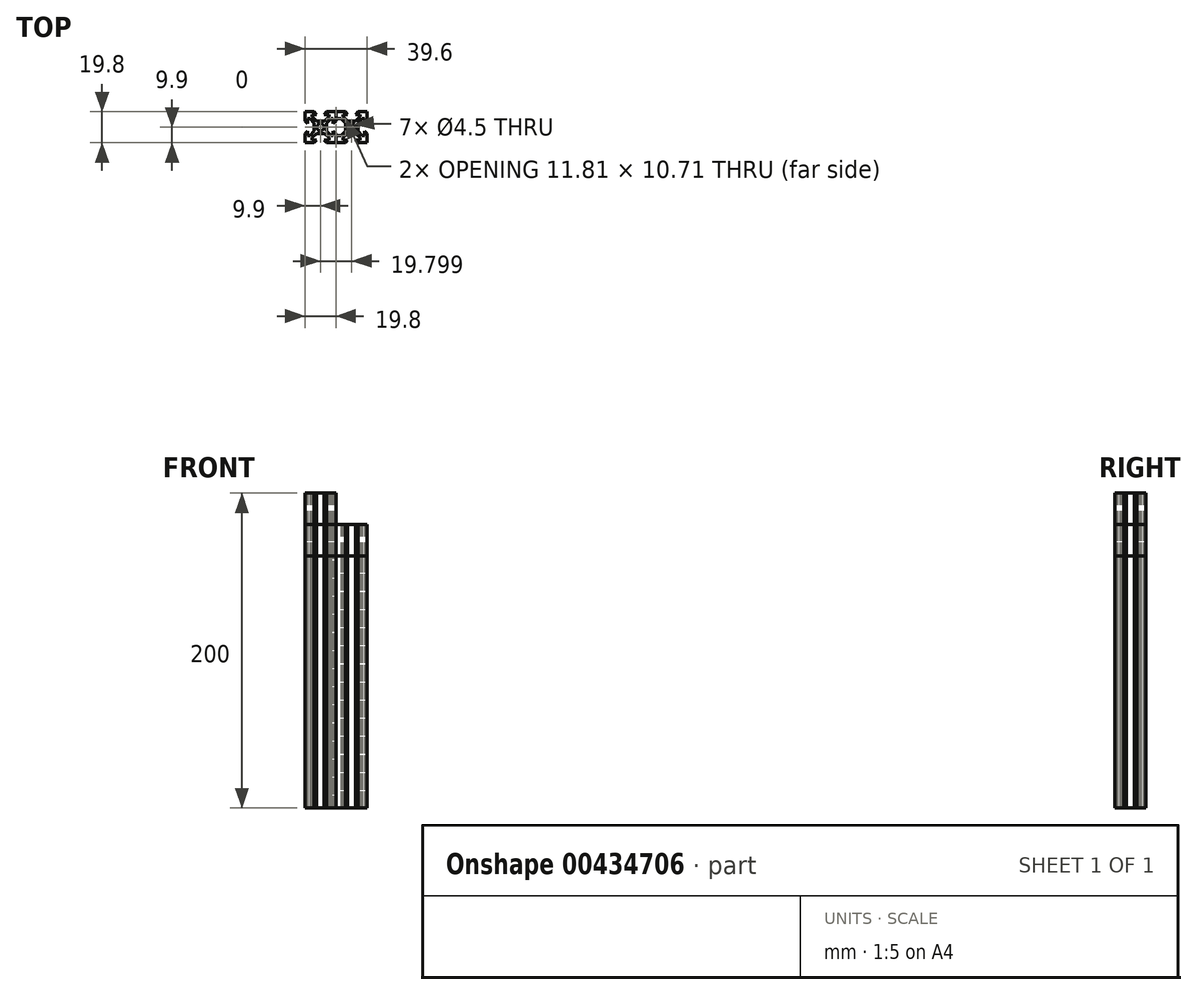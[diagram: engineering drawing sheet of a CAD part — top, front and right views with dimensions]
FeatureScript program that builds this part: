
annotation { "Feature Type Name" : "Feature", "Feature Type Description" : "" }
export const myFeature = defineFeature(function(context is Context, id is Id, definition is map)
    precondition{}
    {
        {
            assignVariable(context, id + "F0", {"name" : "Length", "anyValue" : 180});
        }
        {
            var Q0;
            Q0=qCreatedBy(makeId("Top.planeOp"),FACE);
            var sketch = newSketch(context, id + "F1", { "sketchPlane" : qUnion([Q0])});
            skCircle(sketch, "E0", {"center": v(0, 0) * mm, "radius": 2.25 * mm});
            skLineSegment(sketch, "E1", {"start": v(0, 82.59) * mm, "end": v(0, 0) * mm, "construction": true});
            skLineSegment(sketch, "E2", {"start": v(0, 0) * mm, "end": v(0, -82.59) * mm, "construction": true});
            skLineSegment(sketch, "E3", {"start": v(0, 0) * mm, "end": v(82.59, 0) * mm, "construction": true});
            skLineSegment(sketch, "E4", {"start": v(0, 0) * mm, "end": v(-82.59, 0) * mm, "construction": true});
            skLineSegment(sketch, "E5", {"start": v(0, 0) * mm, "end": v(-82.59, 82.59) * mm, "construction": true});
            skLineSegment(sketch, "E6", {"start": v(0, 0) * mm, "end": v(82.59, -82.59) * mm, "construction": true});
            skLineSegment(sketch, "E7", {"start": v(0, 0) * mm, "end": v(82.59, 82.59) * mm, "construction": true});
            skLineSegment(sketch, "E8", {"start": v(0, 0) * mm, "end": v(-82.59, -82.59) * mm, "construction": true});
            skLineSegment(sketch, "E9", {"start": v(-82.59, 82.59) * mm, "end": v(82.59, 82.59) * mm, "construction": true});
            skLineSegment(sketch, "E10", {"start": v(-82.59, -82.59) * mm, "end": v(82.59, -82.59) * mm, "construction": true});
            skLineSegment(sketch, "E11", {"start": v(-82.59, -82.59) * mm, "end": v(-82.59, 82.59) * mm, "construction": true});
            skLineSegment(sketch, "E12", {"start": v(82.59, -82.59) * mm, "end": v(82.59, 82.59) * mm, "construction": true});
            skPoint(sketch, "E13", {"position": v(-6.72, 6.72) * mm});
            skPoint(sketch, "E14", {"position": v(-4, 4) * mm});
            skPoint(sketch, "E15", {"position": v(-8.13, 8.13) * mm});
            skPoint(sketch, "E16", {"position": v(-47.98, 47.98) * mm});
            skPoint(sketch, "E17", {"position": v(-56.83, 56.83) * mm});
            skPoint(sketch, "E18", {"position": v(-9.9, 9.9) * mm});
            skLineSegment(sketch, "E19.bottom", {"start": v(-9.9, 9.9) * mm, "end": v(0, 9.9) * mm, "construction": true});
            skLineSegment(sketch, "E19.top", {"start": v(-9.9, 0) * mm, "end": v(0, 0) * mm, "construction": true});
            skLineSegment(sketch, "E19.left", {"start": v(-9.9, 9.9) * mm, "end": v(-9.9, 0) * mm, "construction": true});
            skLineSegment(sketch, "E19.right", {"start": v(0, 9.9) * mm, "end": v(0, 0) * mm, "construction": true});
            skLineSegment(sketch, "E20.MirrorCS", {"start": v(9.9, 9.9) * mm, "end": v(0, 9.9) * mm, "construction": true});
            skLineSegment(sketch, "E21.MirrorCS", {"start": v(9.9, 9.9) * mm, "end": v(9.9, 0) * mm, "construction": true});
            skLineSegment(sketch, "E22.MirrorCS", {"start": v(-9.9, -9.9) * mm, "end": v(-9.9, 0) * mm, "construction": true});
            skLineSegment(sketch, "E23.MirrorCS", {"start": v(-9.9, -9.9) * mm, "end": v(0, -9.9) * mm, "construction": true});
            skLineSegment(sketch, "E24.MirrorCS", {"start": v(9.9, -9.9) * mm, "end": v(0, -9.9) * mm, "construction": true});
            skLineSegment(sketch, "E25.MirrorCS", {"start": v(9.9, -9.9) * mm, "end": v(9.9, 0) * mm, "construction": true});
            skLineSegment(sketch, "E26.bottom", {"start": v(-4, 4) * mm, "end": v(0, 4) * mm, "construction": true});
            skLineSegment(sketch, "E26.top", {"start": v(-4, 0) * mm, "end": v(0, 0) * mm, "construction": true});
            skLineSegment(sketch, "E26.left", {"start": v(-4, 4) * mm, "end": v(-4, 0) * mm, "construction": true});
            skLineSegment(sketch, "E26.right", {"start": v(0, 4) * mm, "end": v(0, 0) * mm, "construction": true});
            skLineSegment(sketch, "E27.bottom", {"start": v(-6.72, 6.72) * mm, "end": v(0, 6.72) * mm, "construction": true});
            skLineSegment(sketch, "E27.top", {"start": v(-6.72, 0) * mm, "end": v(0, 0) * mm, "construction": true});
            skLineSegment(sketch, "E27.left", {"start": v(-6.72, 6.72) * mm, "end": v(-6.72, 0) * mm, "construction": true});
            skLineSegment(sketch, "E27.right", {"start": v(0, 6.72) * mm, "end": v(0, 0) * mm, "construction": true});
            skLineSegment(sketch, "E28.MirrorCS", {"start": v(4, 4) * mm, "end": v(0, 4) * mm, "construction": true});
            skLineSegment(sketch, "E29.MirrorCS", {"start": v(6.72, 6.72) * mm, "end": v(0, 6.72) * mm, "construction": true});
            skLineSegment(sketch, "E30.MirrorCS", {"start": v(6.72, 6.72) * mm, "end": v(6.72, 0) * mm, "construction": true});
            skLineSegment(sketch, "E31.MirrorCS", {"start": v(4, 4) * mm, "end": v(4, 0) * mm, "construction": true});
            skLineSegment(sketch, "E32.MirrorCS", {"start": v(-6.72, -6.72) * mm, "end": v(-6.72, 0) * mm, "construction": true});
            skLineSegment(sketch, "E33.MirrorCS", {"start": v(-4, -4) * mm, "end": v(-4, 0) * mm, "construction": true});
            skLineSegment(sketch, "E34.MirrorCS", {"start": v(-6.72, -6.72) * mm, "end": v(0, -6.72) * mm, "construction": true});
            skLineSegment(sketch, "E35.MirrorCS", {"start": v(-4, -4) * mm, "end": v(0, -4) * mm, "construction": true});
            skLineSegment(sketch, "E36.MirrorCS", {"start": v(4, -4) * mm, "end": v(0, -4) * mm, "construction": true});
            skLineSegment(sketch, "E37.MirrorCS", {"start": v(6.72, -6.72) * mm, "end": v(0, -6.72) * mm, "construction": true});
            skLineSegment(sketch, "E38.MirrorCS", {"start": v(6.72, -6.72) * mm, "end": v(6.72, 0) * mm, "construction": true});
            skLineSegment(sketch, "E39.MirrorCS", {"start": v(4, -4) * mm, "end": v(4, 0) * mm, "construction": true});
            skLineSegment(sketch, "E40.bottom", {"start": v(-6.72, 6.72) * mm, "end": v(-4, 6.72) * mm, "construction": true});
            skLineSegment(sketch, "E40.top", {"start": v(-6.72, 4) * mm, "end": v(-4, 4) * mm, "construction": true});
            skLineSegment(sketch, "E40.left", {"start": v(-6.72, 6.72) * mm, "end": v(-6.72, 4) * mm, "construction": true});
            skLineSegment(sketch, "E40.right", {"start": v(-4, 6.72) * mm, "end": v(-4, 4) * mm, "construction": true});
            skLineSegment(sketch, "E41.bottom", {"start": v(-9.9, 9.9) * mm, "end": v(-6.72, 9.9) * mm, "construction": true});
            skLineSegment(sketch, "E41.top", {"start": v(-9.9, 6.72) * mm, "end": v(-6.72, 6.72) * mm, "construction": true});
            skLineSegment(sketch, "E41.left", {"start": v(-9.9, 9.9) * mm, "end": v(-9.9, 6.72) * mm, "construction": true});
            skLineSegment(sketch, "E41.right", {"start": v(-6.72, 9.9) * mm, "end": v(-6.72, 6.72) * mm, "construction": true});
            skPoint(sketch, "E42.oppositeSnap0", {"position": v(-6.72, 5.36) * mm});
            skLineSegment(sketch, "E42.bottom", {"start": v(-9.9, 9.9) * mm, "end": v(-5.36, 9.9) * mm, "construction": true});
            skLineSegment(sketch, "E42.top", {"start": v(-9.9, 5.36) * mm, "end": v(-5.36, 5.36) * mm, "construction": true});
            skLineSegment(sketch, "E42.left", {"start": v(-9.9, 9.9) * mm, "end": v(-9.9, 5.36) * mm, "construction": true});
            skLineSegment(sketch, "E42.right", {"start": v(-5.36, 9.9) * mm, "end": v(-5.36, 5.36) * mm, "construction": true});
            skLineSegment(sketch, "E43.bottom", {"start": v(-5.36, 5.36) * mm, "end": v(-2.5, 5.36) * mm, "construction": true});
            skLineSegment(sketch, "E43.top", {"start": v(-5.36, 2.5) * mm, "end": v(-2.5, 2.5) * mm, "construction": true});
            skLineSegment(sketch, "E43.left", {"start": v(-5.36, 5.36) * mm, "end": v(-5.36, 2.5) * mm, "construction": true});
            skLineSegment(sketch, "E43.right", {"start": v(-2.5, 5.36) * mm, "end": v(-2.5, 2.5) * mm, "construction": true});
            skPoint(sketch, "E44", {"position": v(-5.36, 6.72) * mm});
            skPoint(sketch, "E45", {"position": v(-2.5, 4) * mm});
            skPoint(sketch, "E46", {"position": v(-4, 2.5) * mm});
            skPoint(sketch, "E47.MirrorP", {"position": v(5.36, 6.72) * mm});
            skPoint(sketch, "E48.MirrorP", {"position": v(2.5, 4) * mm});
            skPoint(sketch, "E49.MirrorP", {"position": v(4, 2.5) * mm});
            skPoint(sketch, "E50.MirrorP", {"position": v(6.72, 5.36) * mm});
            skPoint(sketch, "E51.MirrorP", {"position": v(-6.72, -5.36) * mm});
            skPoint(sketch, "E52.MirrorP", {"position": v(-4, -2.5) * mm});
            skPoint(sketch, "E53.MirrorP", {"position": v(-2.5, -4) * mm});
            skPoint(sketch, "E54.MirrorP", {"position": v(-5.36, -6.72) * mm});
            skPoint(sketch, "E55.MirrorP", {"position": v(2.5, -4) * mm});
            skPoint(sketch, "E56.MirrorP", {"position": v(5.36, -6.72) * mm});
            skPoint(sketch, "E57.MirrorP", {"position": v(6.72, -5.36) * mm});
            skPoint(sketch, "E58.MirrorP", {"position": v(4, -2.5) * mm});
            skLineSegment(sketch, "E59", {"start": v(-2.5, 4) * mm, "end": v(2.5, 4) * mm});
            skLineSegment(sketch, "E60", {"start": v(-4, 2.5) * mm, "end": v(-4, -2.5) * mm});
            skLineSegment(sketch, "E61", {"start": v(4, 2.5) * mm, "end": v(4, -2.5) * mm});
            skLineSegment(sketch, "E62", {"start": v(2.5, -4) * mm, "end": v(-2.5, -4) * mm});
            skLineSegment(sketch, "E63", {"start": v(-2.5, 4) * mm, "end": v(-5.36, 6.72) * mm});
            skLineSegment(sketch, "E64", {"start": v(-4, 2.5) * mm, "end": v(-6.72, 5.36) * mm});
            skLineSegment(sketch, "E65", {"start": v(2.5, 4) * mm, "end": v(5.36, 6.72) * mm});
            skLineSegment(sketch, "E66", {"start": v(6.72, 5.36) * mm, "end": v(4, 2.5) * mm});
            skLineSegment(sketch, "E67", {"start": v(4, -2.5) * mm, "end": v(6.72, -5.36) * mm});
            skLineSegment(sketch, "E68", {"start": v(5.36, -6.72) * mm, "end": v(2.5, -4) * mm});
            skLineSegment(sketch, "E69", {"start": v(-2.5, -4) * mm, "end": v(-5.36, -6.72) * mm});
            skLineSegment(sketch, "E70", {"start": v(-6.72, -5.36) * mm, "end": v(-4, -2.5) * mm});
            skPoint(sketch, "E71", {"position": v(-2.5, 6.72) * mm});
            skPoint(sketch, "E72", {"position": v(-4, 9.9) * mm});
            skPoint(sketch, "E73.MirrorP", {"position": v(8.13, 8.13) * mm});
            skPoint(sketch, "E74.MirrorP", {"position": v(9.9, 9.9) * mm});
            skPoint(sketch, "E75.MirrorP", {"position": v(-8.13, -8.13) * mm});
            skPoint(sketch, "E76.MirrorP", {"position": v(8.13, -8.13) * mm});
            skPoint(sketch, "E77.MirrorP", {"position": v(9.9, -9.9) * mm});
            skPoint(sketch, "E78.MirrorP", {"position": v(-9.9, -9.9) * mm});
            skLineSegment(sketch, "E79.bottom", {"start": v(-8.13, 8.13) * mm, "end": v(8.13, 8.13) * mm, "construction": true});
            skLineSegment(sketch, "E79.top", {"start": v(-8.13, -8.13) * mm, "end": v(8.13, -8.13) * mm, "construction": true});
            skLineSegment(sketch, "E79.left", {"start": v(-8.13, 8.13) * mm, "end": v(-8.13, -8.13) * mm, "construction": true});
            skLineSegment(sketch, "E79.right", {"start": v(8.13, 8.13) * mm, "end": v(8.13, -8.13) * mm, "construction": true});
            skPoint(sketch, "E80", {"position": v(0, 5.36) * mm});
            skLineSegment(sketch, "E81", {"start": v(-4, 9.9) * mm, "end": v(0, 5.36) * mm, "construction": true});
            skPoint(sketch, "E82", {"position": v(-5.36, 8.13) * mm});
            skPoint(sketch, "E83", {"position": v(-8.13, 5.36) * mm});
            skPoint(sketch, "E84.MirrorP", {"position": v(-5.36, 0) * mm});
            skLineSegment(sketch, "E85.MirrorCS", {"start": v(-9.9, 4) * mm, "end": v(-5.36, 0) * mm, "construction": true});
            skPoint(sketch, "E86", {"position": v(-2.44, 8.13) * mm});
            skPoint(sketch, "E87", {"position": v(-8.13, 2.44) * mm});
            skLineSegment(sketch, "E88.MirrorCS", {"start": v(5.36, 5.36) * mm, "end": v(2.5, 5.36) * mm, "construction": true});
            skLineSegment(sketch, "E89.MirrorCS", {"start": v(2.5, 5.36) * mm, "end": v(2.5, 2.5) * mm, "construction": true});
            skLineSegment(sketch, "E90", {"start": v(-2.44, 8.13) * mm, "end": v(-5.36, 8.13) * mm});
            skLineSegment(sketch, "E91", {"start": v(-5.36, 8.13) * mm, "end": v(-5.36, 6.72) * mm});
            skLineSegment(sketch, "E92", {"start": v(-2.44, 8.13) * mm, "end": v(-4, 9.9) * mm});
            skLineSegment(sketch, "E93", {"start": v(-4, 9.9) * mm, "end": v(-9.9, 9.9) * mm});
            skLineSegment(sketch, "E94", {"start": v(-9.9, 9.9) * mm, "end": v(-9.9, 4) * mm});
            skLineSegment(sketch, "E95", {"start": v(-9.9, 4) * mm, "end": v(-8.13, 2.44) * mm});
            skLineSegment(sketch, "E96", {"start": v(-8.13, 2.44) * mm, "end": v(-8.13, 5.36) * mm});
            skLineSegment(sketch, "E97", {"start": v(-8.13, 5.36) * mm, "end": v(-6.72, 5.36) * mm});
            skLineSegment(sketch, "E98.MirrorCS", {"start": v(2.44, 8.13) * mm, "end": v(4, 9.9) * mm});
            skLineSegment(sketch, "E99.MirrorCS", {"start": v(4, 9.9) * mm, "end": v(9.9, 9.9) * mm});
            skLineSegment(sketch, "E100.MirrorCS", {"start": v(2.44, 8.13) * mm, "end": v(5.36, 8.13) * mm});
            skLineSegment(sketch, "E101.MirrorCS", {"start": v(5.36, 8.13) * mm, "end": v(5.36, 6.72) * mm});
            skLineSegment(sketch, "E102.MirrorCS", {"start": v(9.9, 9.9) * mm, "end": v(9.9, 4) * mm});
            skLineSegment(sketch, "E103.MirrorCS", {"start": v(9.9, 4) * mm, "end": v(8.13, 2.44) * mm});
            skLineSegment(sketch, "E104.MirrorCS", {"start": v(8.13, 2.44) * mm, "end": v(8.13, 5.36) * mm});
            skLineSegment(sketch, "E105.MirrorCS", {"start": v(8.13, 5.36) * mm, "end": v(6.72, 5.36) * mm});
            skLineSegment(sketch, "E106.MirrorCS", {"start": v(-9.9, -4) * mm, "end": v(-8.13, -2.44) * mm});
            skLineSegment(sketch, "E107.MirrorCS", {"start": v(9.9, -4) * mm, "end": v(8.13, -2.44) * mm});
            skLineSegment(sketch, "E108.MirrorCS", {"start": v(8.13, -2.44) * mm, "end": v(8.13, -5.36) * mm});
            skLineSegment(sketch, "E109.MirrorCS", {"start": v(-8.13, -2.44) * mm, "end": v(-8.13, -5.36) * mm});
            skLineSegment(sketch, "E110.MirrorCS", {"start": v(-9.9, -9.9) * mm, "end": v(-9.9, -4) * mm});
            skPoint(sketch, "E111.MirrorP", {"position": v(-4, -9.9) * mm});
            skLineSegment(sketch, "E112.MirrorCS", {"start": v(-4, -9.9) * mm, "end": v(-9.9, -9.9) * mm});
            skPoint(sketch, "E113.MirrorP", {"position": v(-2.44, -8.13) * mm});
            skPoint(sketch, "E114.MirrorP", {"position": v(-5.36, -8.13) * mm});
            skLineSegment(sketch, "E115.MirrorCS", {"start": v(-2.44, -8.13) * mm, "end": v(-5.36, -8.13) * mm});
            skLineSegment(sketch, "E116.MirrorCS", {"start": v(-5.36, -8.13) * mm, "end": v(-5.36, -6.72) * mm});
            skPoint(sketch, "E117.MirrorP", {"position": v(-8.13, -5.36) * mm});
            skLineSegment(sketch, "E118.MirrorCS", {"start": v(-8.13, -5.36) * mm, "end": v(-6.72, -5.36) * mm});
            skLineSegment(sketch, "E119.MirrorCS", {"start": v(-2.44, -8.13) * mm, "end": v(-4, -9.9) * mm});
            skLineSegment(sketch, "E120.MirrorCS", {"start": v(9.9, -9.9) * mm, "end": v(9.9, -4) * mm});
            skLineSegment(sketch, "E121.MirrorCS", {"start": v(4, -9.9) * mm, "end": v(9.9, -9.9) * mm});
            skLineSegment(sketch, "E122.MirrorCS", {"start": v(2.44, -8.13) * mm, "end": v(4, -9.9) * mm});
            skLineSegment(sketch, "E123.MirrorCS", {"start": v(2.44, -8.13) * mm, "end": v(5.36, -8.13) * mm});
            skLineSegment(sketch, "E124.MirrorCS", {"start": v(5.36, -8.13) * mm, "end": v(5.36, -6.72) * mm});
            skLineSegment(sketch, "E125.MirrorCS", {"start": v(8.13, -5.36) * mm, "end": v(6.72, -5.36) * mm});
            skSolve(sketch);
        }
        {
            var Q0;
            Q0=qSketchRegion(id+"F1",true);
            extrude(context, id + "F2", {"entities" : qUnion([Q0]), "depth" : (getVariable(context, 'Length')) * mm});
        }
        {
            var Q0;
            Q0=qSketchRegion(id+"F1",true);
            extrude(context, id + "F3", {"entities" : qUnion([Q0]), "depth" : 180 * mm});
        }
        {
            var Q0;
            Q0=qSketchRegion(id+"F1",true);
            extrude(context, id + "F4", {"entities" : qUnion([Q0]), "depth" : 200 * mm});
        }
        {
            var Q0;
            Q0=qCreatedBy(makeId("Top.planeOp"),FACE);
            var sketch = newSketch(context, id + "F5", { "sketchPlane" : qUnion([Q0])});
            skLineSegment(sketch, "E126.0", {"start": v(4, 9.9) * mm, "end": v(9.9, 9.9) * mm});
            skLineSegment(sketch, "E126.1", {"start": v(2.44, 8.13) * mm, "end": v(4, 9.9) * mm});
            skLineSegment(sketch, "E126.2", {"start": v(2.44, 8.13) * mm, "end": v(5.36, 8.13) * mm});
            skLineSegment(sketch, "E126.3", {"start": v(5.36, 8.13) * mm, "end": v(5.36, 6.72) * mm});
            skLineSegment(sketch, "E126.4", {"start": v(6.72, 5.36) * mm, "end": v(4, 2.5) * mm});
            skLineSegment(sketch, "E126.5", {"start": v(2.5, 4) * mm, "end": v(5.36, 6.72) * mm});
            skLineSegment(sketch, "E126.6", {"start": v(-2.5, 4) * mm, "end": v(2.5, 4) * mm});
            skLineSegment(sketch, "E126.7", {"start": v(-2.5, 4) * mm, "end": v(-5.36, 6.72) * mm});
            skLineSegment(sketch, "E126.8", {"start": v(-2.44, 8.13) * mm, "end": v(-5.36, 8.13) * mm});
            skLineSegment(sketch, "E126.9", {"start": v(-2.44, 8.13) * mm, "end": v(-4, 9.9) * mm});
            skLineSegment(sketch, "E126.10", {"start": v(-4, 9.9) * mm, "end": v(-9.9, 9.9) * mm});
            skLineSegment(sketch, "E126.11", {"start": v(-5.36, 8.13) * mm, "end": v(-5.36, 6.72) * mm});
            skLineSegment(sketch, "E126.12", {"start": v(-9.9, 9.9) * mm, "end": v(-9.9, 4) * mm});
            skLineSegment(sketch, "E126.13", {"start": v(-9.9, 4) * mm, "end": v(-8.13, 2.44) * mm});
            skLineSegment(sketch, "E126.14", {"start": v(-8.13, 2.44) * mm, "end": v(-8.13, 5.36) * mm});
            skLineSegment(sketch, "E126.15", {"start": v(-8.13, 5.36) * mm, "end": v(-6.72, 5.36) * mm});
            skLineSegment(sketch, "E126.16", {"start": v(-4, 2.5) * mm, "end": v(-6.72, 5.36) * mm});
            skLineSegment(sketch, "E126.17", {"start": v(-4, 2.5) * mm, "end": v(-4, -2.5) * mm});
            skLineSegment(sketch, "E126.18", {"start": v(4, 2.5) * mm, "end": v(4, -2.5) * mm});
            skLineSegment(sketch, "E126.19", {"start": v(-6.72, -5.36) * mm, "end": v(-4, -2.5) * mm});
            skLineSegment(sketch, "E126.20", {"start": v(-2.5, -4) * mm, "end": v(-5.36, -6.72) * mm});
            skLineSegment(sketch, "E126.21", {"start": v(-8.13, -2.44) * mm, "end": v(-8.13, -5.36) * mm});
            skLineSegment(sketch, "E126.22", {"start": v(-9.9, -4) * mm, "end": v(-8.13, -2.44) * mm});
            skLineSegment(sketch, "E126.23", {"start": v(-9.9, -9.9) * mm, "end": v(-9.9, -4) * mm});
            skLineSegment(sketch, "E126.24", {"start": v(-4, -9.9) * mm, "end": v(-9.9, -9.9) * mm});
            skLineSegment(sketch, "E126.25", {"start": v(-2.44, -8.13) * mm, "end": v(-5.36, -8.13) * mm});
            skLineSegment(sketch, "E126.26", {"start": v(2.5, -4) * mm, "end": v(-2.5, -4) * mm});
            skLineSegment(sketch, "E126.27", {"start": v(2.44, -8.13) * mm, "end": v(5.36, -8.13) * mm});
            skLineSegment(sketch, "E126.28", {"start": v(2.44, -8.13) * mm, "end": v(4, -9.9) * mm});
            skLineSegment(sketch, "E126.29", {"start": v(4, -9.9) * mm, "end": v(9.9, -9.9) * mm});
            skLineSegment(sketch, "E126.30", {"start": v(4, -2.5) * mm, "end": v(6.72, -5.36) * mm});
            skLineSegment(sketch, "E126.31", {"start": v(5.36, -6.72) * mm, "end": v(2.5, -4) * mm});
            skLineSegment(sketch, "E126.32", {"start": v(-2.44, -8.13) * mm, "end": v(-4, -9.9) * mm});
            skLineSegment(sketch, "E126.33", {"start": v(-5.36, -8.13) * mm, "end": v(-5.36, -6.72) * mm});
            skLineSegment(sketch, "E126.34", {"start": v(-8.13, -5.36) * mm, "end": v(-6.72, -5.36) * mm});
            skLineSegment(sketch, "E126.35", {"start": v(5.36, -8.13) * mm, "end": v(5.36, -6.72) * mm});
            skLineSegment(sketch, "E127.0", {"start": v(9.9, 9.9) * mm, "end": v(9.9, 0) * mm, "construction": true});
            skLineSegment(sketch, "E127.1", {"start": v(9.9, -9.9) * mm, "end": v(9.9, 0) * mm, "construction": true});
            skLineSegment(sketch, "E128.MirrorCS", {"start": v(15.8, 9.9) * mm, "end": v(9.9, 9.9) * mm});
            skLineSegment(sketch, "E129.MirrorCS", {"start": v(17.36, 8.13) * mm, "end": v(15.8, 9.9) * mm});
            skLineSegment(sketch, "E130.MirrorCS", {"start": v(17.36, 8.13) * mm, "end": v(14.44, 8.13) * mm});
            skLineSegment(sketch, "E131.MirrorCS", {"start": v(14.44, 8.13) * mm, "end": v(14.44, 6.72) * mm});
            skLineSegment(sketch, "E132.MirrorCS", {"start": v(17.3, 4) * mm, "end": v(14.44, 6.72) * mm});
            skLineSegment(sketch, "E133.MirrorCS", {"start": v(13.08, 5.36) * mm, "end": v(15.8, 2.5) * mm});
            skLineSegment(sketch, "E134.MirrorCS", {"start": v(15.8, 2.5) * mm, "end": v(15.8, -2.5) * mm});
            skLineSegment(sketch, "E135.MirrorCS", {"start": v(15.8, -2.5) * mm, "end": v(13.08, -5.36) * mm});
            skLineSegment(sketch, "E136.MirrorCS", {"start": v(22.3, 4) * mm, "end": v(17.3, 4) * mm});
            skLineSegment(sketch, "E137.MirrorCS", {"start": v(22.3, 4) * mm, "end": v(25.16, 6.72) * mm});
            skLineSegment(sketch, "E138.MirrorCS", {"start": v(22.24, 8.13) * mm, "end": v(25.16, 8.13) * mm});
            skLineSegment(sketch, "E139.MirrorCS", {"start": v(22.24, 8.13) * mm, "end": v(23.8, 9.9) * mm});
            skLineSegment(sketch, "E140.MirrorCS", {"start": v(23.8, 9.9) * mm, "end": v(29.7, 9.9) * mm});
            skLineSegment(sketch, "E141.MirrorCS", {"start": v(25.16, 8.13) * mm, "end": v(25.16, 6.72) * mm});
            skLineSegment(sketch, "E142.MirrorCS", {"start": v(23.8, 2.5) * mm, "end": v(26.52, 5.36) * mm});
            skLineSegment(sketch, "E143.MirrorCS", {"start": v(27.93, 5.36) * mm, "end": v(26.52, 5.36) * mm});
            skLineSegment(sketch, "E144.MirrorCS", {"start": v(29.7, 9.9) * mm, "end": v(29.7, 4) * mm});
            skLineSegment(sketch, "E145.MirrorCS", {"start": v(29.7, 4) * mm, "end": v(27.93, 2.44) * mm});
            skLineSegment(sketch, "E146.MirrorCS", {"start": v(23.8, 2.5) * mm, "end": v(23.8, -2.5) * mm});
            skLineSegment(sketch, "E147.MirrorCS", {"start": v(26.52, -5.36) * mm, "end": v(23.8, -2.5) * mm});
            skLineSegment(sketch, "E148.MirrorCS", {"start": v(22.3, -4) * mm, "end": v(25.16, -6.72) * mm});
            skLineSegment(sketch, "E149.MirrorCS", {"start": v(17.3, -4) * mm, "end": v(22.3, -4) * mm});
            skLineSegment(sketch, "E150.MirrorCS", {"start": v(27.93, -5.36) * mm, "end": v(26.52, -5.36) * mm});
            skLineSegment(sketch, "E151.MirrorCS", {"start": v(29.7, -4) * mm, "end": v(27.93, -2.44) * mm});
            skLineSegment(sketch, "E152.MirrorCS", {"start": v(29.7, -9.9) * mm, "end": v(29.7, -4) * mm});
            skLineSegment(sketch, "E153.MirrorCS", {"start": v(14.44, -6.72) * mm, "end": v(17.3, -4) * mm});
            skLineSegment(sketch, "E154.MirrorCS", {"start": v(14.44, -8.13) * mm, "end": v(14.44, -6.72) * mm});
            skLineSegment(sketch, "E155.MirrorCS", {"start": v(17.36, -8.13) * mm, "end": v(14.44, -8.13) * mm});
            skLineSegment(sketch, "E156.MirrorCS", {"start": v(17.36, -8.13) * mm, "end": v(15.8, -9.9) * mm});
            skLineSegment(sketch, "E157.MirrorCS", {"start": v(15.8, -9.9) * mm, "end": v(9.9, -9.9) * mm});
            skLineSegment(sketch, "E158.MirrorCS", {"start": v(22.24, -8.13) * mm, "end": v(23.8, -9.9) * mm});
            skLineSegment(sketch, "E159.MirrorCS", {"start": v(22.24, -8.13) * mm, "end": v(25.16, -8.13) * mm});
            skLineSegment(sketch, "E160.MirrorCS", {"start": v(25.16, -8.13) * mm, "end": v(25.16, -6.72) * mm});
            skLineSegment(sketch, "E161.MirrorCS", {"start": v(23.8, -9.9) * mm, "end": v(29.7, -9.9) * mm});
            skLineSegment(sketch, "E162.MirrorCS", {"start": v(27.93, -2.44) * mm, "end": v(27.93, -5.36) * mm});
            skLineSegment(sketch, "E163.MirrorCS", {"start": v(27.93, 2.44) * mm, "end": v(27.93, 5.36) * mm});
            skLineSegment(sketch, "E164", {"start": v(6.72, 5.36) * mm, "end": v(13.08, 5.36) * mm});
            skLineSegment(sketch, "E165", {"start": v(13.08, -5.36) * mm, "end": v(6.72, -5.36) * mm});
            skCircle(sketch, "E166.0", {"center": v(0, 0) * mm, "radius": 2.25 * mm});
            skCircle(sketch, "E167.MirrorC", {"center": v(19.8, 0) * mm, "radius": 2.25 * mm});
            skSolve(sketch);
        }
        {
            var Q0;
            Q0=makeQuery(id+"F5.imprint","IMPRINT",FACE,{"disambiguationData":[TD([[makeQuery(id+"F5.imprint","IMPRINT",EDGE,{"derivedFrom":sQuery(id+"F5.wireOp",EDGE,"E126.0")}),-1.0]])]});
            extrude(context, id + "F6", {"entities" : qUnion([Q0]), "depth" : (getVariable(context, 'Length')) * mm});
        }
        {
            var Q0;
            Q0=qSketchRegion(id+"F5",true);
            extrude(context, id + "F7", {"entities" : qUnion([Q0]), "depth" : 160 * mm});
        }
    });
